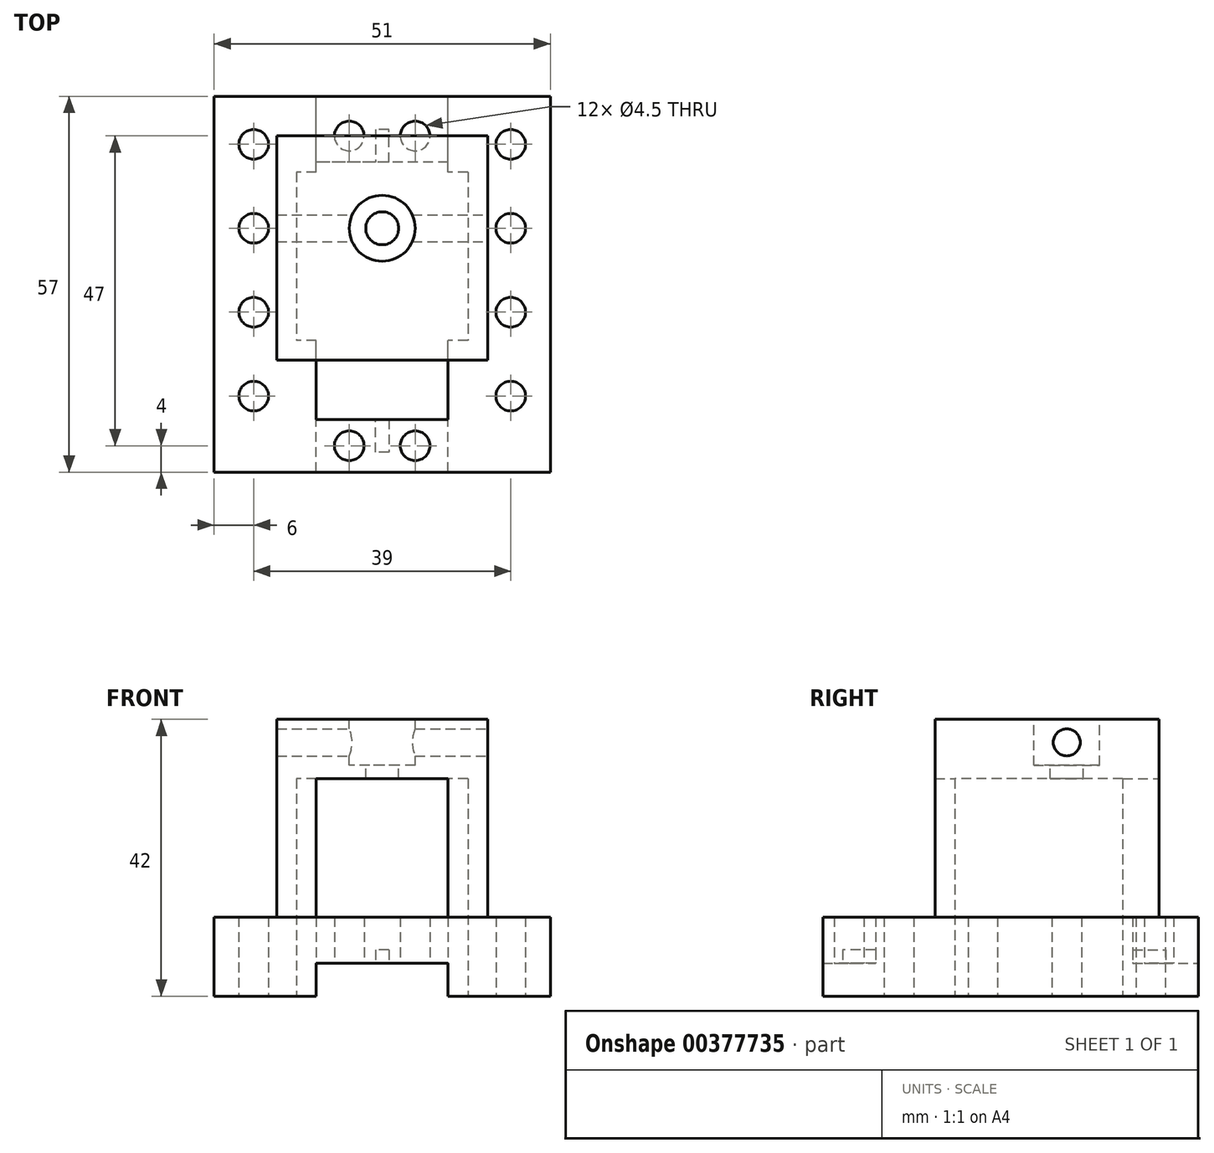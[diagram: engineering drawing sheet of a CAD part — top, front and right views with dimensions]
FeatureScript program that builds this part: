
annotation { "Feature Type Name" : "Feature", "Feature Type Description" : "" }
export const myFeature = defineFeature(function(context is Context, id is Id, definition is map)
    precondition{}
    {
        {
            var Q0;
            Q0=qCreatedBy(makeId("Top.planeOp"),FACE);
            var sketch = newSketch(context, id + "F0", { "sketchPlane" : qUnion([Q0])});
            skLineSegment(sketch, "E0.bottom", {"start": v(0, 0) * mm, "end": v(51, 0) * mm});
            skLineSegment(sketch, "E0.top", {"start": v(0, -55) * mm, "end": v(51, -55) * mm});
            skLineSegment(sketch, "E0.left", {"start": v(0, 0) * mm, "end": v(0, -55) * mm});
            skLineSegment(sketch, "E0.right", {"start": v(51, 0) * mm, "end": v(51, -55) * mm});
            skPoint(sketch, "E1", {"position": v(35.5, -55) * mm});
            skPoint(sketch, "E2", {"position": v(15.5, -55) * mm});
            skLineSegment(sketch, "E3", {"start": v(15.5, -55) * mm, "end": v(15.5, 0) * mm});
            skLineSegment(sketch, "E4", {"start": v(35.5, -55) * mm, "end": v(35.5, 0) * mm});
            skPoint(sketch, "E5", {"position": v(15.5, -47) * mm});
            skPoint(sketch, "E6", {"position": v(35.5, -47) * mm});
            skPoint(sketch, "E7", {"position": v(35.5, -8) * mm});
            skPoint(sketch, "E8", {"position": v(15.5, -8) * mm});
            skLineSegment(sketch, "E9", {"start": v(15.5, -47) * mm, "end": v(35.5, -47) * mm});
            skLineSegment(sketch, "E10", {"start": v(35.5, -8) * mm, "end": v(15.5, -8) * mm});
            skPoint(sketch, "E11", {"position": v(45, -55) * mm});
            skPoint(sketch, "E12", {"position": v(6, -55) * mm});
            skLineSegment(sketch, "E13", {"start": v(45, -55) * mm, "end": v(45, 0) * mm});
            skLineSegment(sketch, "E14", {"start": v(6, -55) * mm, "end": v(6, 0) * mm});
            skPoint(sketch, "E15", {"position": v(45, -18) * mm});
            skPoint(sketch, "E16", {"position": v(45, -30.73) * mm});
            skPoint(sketch, "E17", {"position": v(45, -5.27) * mm});
            skPoint(sketch, "E18", {"position": v(6, -18) * mm});
            skPoint(sketch, "E19", {"position": v(45, -43.46) * mm});
            skPoint(sketch, "E20", {"position": v(6, -43.46) * mm});
            skPoint(sketch, "E21", {"position": v(6, -30.73) * mm});
            skPoint(sketch, "E22", {"position": v(6, -5.27) * mm});
            skCircle(sketch, "E23", {"center": v(45, -43.46) * mm, "radius": 2.25 * mm});
            skCircle(sketch, "E24", {"center": v(45, -30.73) * mm, "radius": 2.25 * mm});
            skCircle(sketch, "E25", {"center": v(45, -18) * mm, "radius": 2.25 * mm});
            skCircle(sketch, "E26", {"center": v(45, -5.27) * mm, "radius": 2.25 * mm});
            skCircle(sketch, "E27", {"center": v(6, -43.46) * mm, "radius": 2.25 * mm});
            skCircle(sketch, "E28", {"center": v(6, -30.73) * mm, "radius": 2.25 * mm});
            skCircle(sketch, "E29", {"center": v(6, -18) * mm, "radius": 2.25 * mm});
            skCircle(sketch, "E30", {"center": v(6, -5.27) * mm, "radius": 2.25 * mm});
            skPoint(sketch, "E31", {"position": v(35.5, -9.5) * mm});
            skPoint(sketch, "E32", {"position": v(15.5, -9.5) * mm});
            skPoint(sketch, "E33", {"position": v(35.5, -35) * mm});
            skPoint(sketch, "E34", {"position": v(15.5, -35) * mm});
            skPoint(sketch, "E35", {"position": v(38.5, -9.5) * mm});
            skPoint(sketch, "E36", {"position": v(12.5, -35) * mm});
            skLineSegment(sketch, "E37.bottom", {"start": v(38.5, -9.5) * mm, "end": v(12.5, -9.5) * mm});
            skLineSegment(sketch, "E37.top", {"start": v(38.5, -35) * mm, "end": v(12.5, -35) * mm});
            skLineSegment(sketch, "E37.left", {"start": v(38.5, -9.5) * mm, "end": v(38.5, -35) * mm});
            skLineSegment(sketch, "E37.right", {"start": v(12.5, -9.5) * mm, "end": v(12.5, -35) * mm});
            skSolve(sketch);
        }
        {
            var Q0;
            {var subQ5=sQuery(id+"F0.wireOp",EDGE,"E10");Q0=makeQuery(id+"F0.imprint","IMPRINT",FACE,{"disambiguationData":[TD([[makeQuery(id+"F0.imprint","IMPRINT",EDGE,{"derivedFrom":subQ5}),-1.0]])]});}
            var Q1;
            {var subQ5=sQuery(id+"F0.wireOp",EDGE,"E9");Q1=makeQuery(id+"F0.imprint","IMPRINT",FACE,{"disambiguationData":[TD([[makeQuery(id+"F0.imprint","IMPRINT",EDGE,{"derivedFrom":subQ5}),-1.0]])]});}
            var Q2;
            {var subQ0=sQuery(id+"F0.wireOp",EDGE,"E0.left");Q2=makeQuery(id+"F0.imprint","IMPRINT",FACE,{"disambiguationData":[TD([[makeQuery(id+"F0.imprint","IMPRINT",EDGE,{"derivedFrom":subQ0}),1.0]])]});}
            var Q3;
            {var subQ4=sQuery(id+"F0.wireOp",EDGE,"E0.right");Q3=makeQuery(id+"F0.imprint","IMPRINT",FACE,{"disambiguationData":[TD([[makeQuery(id+"F0.imprint","IMPRINT",EDGE,{"derivedFrom":subQ4}),-1.0]])]});}
            var Q4;
            {var subQ1=sQuery(id+"F0.wireOp",EDGE,"E0.bottom");var subQ5=sQuery(id+"F0.wireOp",EDGE,"E3");var subQ6=makeQuery(id+"F0.imprint","INTERSECT",VERTEX,{"derivedFrom":[subQ1,subQ5]});Q4=makeQuery(id+"F0.imprint","IMPRINT",FACE,{"disambiguationData":[TD([[makeQuery(id+"F0.imprint","IMPRINT",EDGE,{"disambiguationData":[TD([[subQ6,1.0]])],"derivedFrom":subQ1}),-1.0]])]});}
            var Q5;
            {var subQ11=sQuery(id+"F0.wireOp",EDGE,"E0.bottom");var subQ15=sQuery(id+"F0.wireOp",EDGE,"E4");var subQ16=makeQuery(id+"F0.imprint","INTERSECT",VERTEX,{"derivedFrom":[subQ11,subQ15]});Q5=makeQuery(id+"F0.imprint","IMPRINT",FACE,{"disambiguationData":[TD([[makeQuery(id+"F0.imprint","IMPRINT",EDGE,{"disambiguationData":[TD([[subQ16,-1.0]])],"derivedFrom":subQ11}),-1.0]])]});}
            extrude(context, id + "F1", {"entities" : qUnion([Q0, Q1, Q2, Q3, Q4, Q5]), "depth" : 12 * mm});
        }
        {
            var Q0;
            {var subQ5=sQuery(id+"F0.wireOp",EDGE,"E9");Q0=makeQuery(id+"F0.imprint","IMPRINT",FACE,{"disambiguationData":[TD([[makeQuery(id+"F0.imprint","IMPRINT",EDGE,{"derivedFrom":subQ5}),-1.0]])]});}
            extrude(context, id + "F2", {"entities" : qUnion([Q0]), "operationType" : NewBodyOperationType.REMOVE, "depth" : 5 * mm});
        }
        {
            var Q0;
            {var subQ5=sQuery(id+"F0.wireOp",EDGE,"E10");Q0=makeQuery(id+"F0.imprint","IMPRINT",FACE,{"disambiguationData":[TD([[makeQuery(id+"F0.imprint","IMPRINT",EDGE,{"derivedFrom":subQ5}),-1.0]])]});}
            extrude(context, id + "F3", {"entities" : qUnion([Q0]), "operationType" : NewBodyOperationType.REMOVE, "depth" : 5 * mm});
        }
        {
            var Q0;
            Q0=makeQuery(id+"F2.boolean.opBoolean","COPY",FACE,{"derivedFrom":makeQuery(id+"F2.opExtrude","CAP_FACE",FACE,{"disambiguationData":[OSD([sQuery(id+"F0.wireOp",EDGE,"E0.top"),sQuery(id+"F0.wireOp",EDGE,"E3"),sQuery(id+"F0.wireOp",EDGE,"E4"),sQuery(id+"F0.wireOp",EDGE,"E9")])],"isStart":false})});
            var sketch = newSketch(context, id + "F4", { "sketchPlane" : qUnion([Q0])});
            skLineSegment(sketch, "E38", {"start": v(25.5, 47) * mm, "end": v(26.5, 47) * mm});
            skLineSegment(sketch, "E39", {"start": v(26.5, 47) * mm, "end": v(26.5, 52) * mm});
            skLineSegment(sketch, "E40", {"start": v(26.5, 52) * mm, "end": v(24.5, 52) * mm});
            skLineSegment(sketch, "E41", {"start": v(24.5, 52) * mm, "end": v(24.5, 47) * mm});
            skLineSegment(sketch, "E42", {"start": v(24.5, 47) * mm, "end": v(25.5, 47) * mm});
            skPoint(sketch, "E43", {"position": v(30.5, 55) * mm});
            skPoint(sketch, "E44", {"position": v(20.5, 55) * mm});
            skPoint(sketch, "E45", {"position": v(30.5, 51) * mm});
            skPoint(sketch, "E46", {"position": v(20.5, 51) * mm});
            skCircle(sketch, "E47", {"center": v(30.5, 51) * mm, "radius": 2.25 * mm});
            skCircle(sketch, "E48", {"center": v(20.5, 51) * mm, "radius": 2.25 * mm});
            skSolve(sketch);
        }
        {
            var Q0;
            Q0=makeQuery(id+"F4.imprint","IMPRINT",FACE,{"disambiguationData":[TD([[makeQuery(id+"F4.imprint","IMPRINT",EDGE,{"derivedFrom":sQuery(id+"F4.wireOp",EDGE,"E38")}),1.0]])]});
            extrude(context, id + "F5", {"entities" : qUnion([Q0]), "operationType" : NewBodyOperationType.REMOVE, "oppositeDirection" : true, "depth" : 2 * mm});
        }
        {
            var Q0;
            Q0=makeQuery(id+"F4.imprint","IMPRINT",FACE,{"disambiguationData":[TD([[makeQuery(id+"F4.imprint","IMPRINT",EDGE,{"derivedFrom":sQuery(id+"F4.wireOp",EDGE,"E48")}),1.0]])]});
            var Q1;
            Q1=makeQuery(id+"F4.imprint","IMPRINT",FACE,{"disambiguationData":[TD([[makeQuery(id+"F4.imprint","IMPRINT",EDGE,{"derivedFrom":sQuery(id+"F4.wireOp",EDGE,"E47")}),1.0]])]});
            extrude(context, id + "F6", {"entities" : qUnion([Q0, Q1]), "operationType" : NewBodyOperationType.REMOVE, "oppositeDirection" : true, "depth" : 25 * mm});
        }
        {
            var Q0;
            Q0=makeQuery(id+"F3.boolean.opBoolean","COPY",FACE,{"derivedFrom":makeQuery(id+"F3.opExtrude","CAP_FACE",FACE,{"disambiguationData":[OSD([sQuery(id+"F0.wireOp",EDGE,"E0.bottom"),sQuery(id+"F0.wireOp",EDGE,"E3"),sQuery(id+"F0.wireOp",EDGE,"E4"),sQuery(id+"F0.wireOp",EDGE,"E10")])],"isStart":false})});
            var sketch = newSketch(context, id + "F7", { "sketchPlane" : qUnion([Q0])});
            skLineSegment(sketch, "E49", {"start": v(25.5, 8) * mm, "end": v(26.5, 8) * mm});
            skLineSegment(sketch, "E50", {"start": v(26.5, 8) * mm, "end": v(26.5, 3) * mm});
            skLineSegment(sketch, "E51", {"start": v(26.5, 3) * mm, "end": v(24.5, 3) * mm});
            skLineSegment(sketch, "E52", {"start": v(24.5, 3) * mm, "end": v(24.5, 8) * mm});
            skLineSegment(sketch, "E53", {"start": v(24.5, 8) * mm, "end": v(25.5, 8) * mm});
            skPoint(sketch, "E54", {"position": v(30.5, 8) * mm});
            skPoint(sketch, "E55", {"position": v(20.5, 8) * mm});
            skPoint(sketch, "E56", {"position": v(30.5, 4) * mm});
            skPoint(sketch, "E57", {"position": v(20.5, 4) * mm});
            skCircle(sketch, "E58", {"center": v(20.5, 4) * mm, "radius": 2.25 * mm});
            skCircle(sketch, "E59", {"center": v(30.5, 4) * mm, "radius": 2.25 * mm});
            skSolve(sketch);
        }
        {
            var Q0;
            Q0=makeQuery(id+"F7.imprint","IMPRINT",FACE,{"disambiguationData":[TD([[makeQuery(id+"F7.imprint","IMPRINT",EDGE,{"derivedFrom":sQuery(id+"F7.wireOp",EDGE,"E49")}),1.0]])]});
            extrude(context, id + "F8", {"entities" : qUnion([Q0]), "operationType" : NewBodyOperationType.REMOVE, "oppositeDirection" : true, "depth" : 2 * mm});
        }
        {
            var Q0;
            Q0=makeQuery(id+"F7.imprint","IMPRINT",FACE,{"disambiguationData":[TD([[makeQuery(id+"F7.imprint","IMPRINT",EDGE,{"derivedFrom":sQuery(id+"F7.wireOp",EDGE,"E59")}),1.0]])]});
            var Q1;
            Q1=makeQuery(id+"F7.imprint","IMPRINT",FACE,{"disambiguationData":[TD([[makeQuery(id+"F7.imprint","IMPRINT",EDGE,{"derivedFrom":sQuery(id+"F7.wireOp",EDGE,"E58")}),1.0]])]});
            extrude(context, id + "F9", {"entities" : qUnion([Q0, Q1]), "operationType" : NewBodyOperationType.REMOVE, "oppositeDirection" : true, "depth" : 25 * mm});
        }
        {
            var Q0;
            Q0=makeQuery(id+"F1.opExtrude","CAP_FACE",FACE,{"disambiguationData":[OSD([sQuery(id+"F0.wireOp",EDGE,"E0.bottom"),sQuery(id+"F0.wireOp",EDGE,"E0.top"),sQuery(id+"F0.wireOp",EDGE,"E0.left"),sQuery(id+"F0.wireOp",EDGE,"E0.right"),sQuery(id+"F0.wireOp",EDGE,"E3"),sQuery(id+"F0.wireOp",EDGE,"E4"),sQuery(id+"F0.wireOp",EDGE,"E9"),sQuery(id+"F0.wireOp",EDGE,"E10"),sQuery(id+"F0.wireOp",EDGE,"E23"),sQuery(id+"F0.wireOp",EDGE,"E24"),sQuery(id+"F0.wireOp",EDGE,"E25"),sQuery(id+"F0.wireOp",EDGE,"E26"),sQuery(id+"F0.wireOp",EDGE,"E27"),sQuery(id+"F0.wireOp",EDGE,"E28"),sQuery(id+"F0.wireOp",EDGE,"E29"),sQuery(id+"F0.wireOp",EDGE,"E30")])],"isStart":false});
            var sketch = newSketch(context, id + "F10", { "sketchPlane" : qUnion([Q0])});
            skPoint(sketch, "E60", {"position": v(9.5, 0) * mm});
            skPoint(sketch, "E61", {"position": v(41.5, 0) * mm});
            skLineSegment(sketch, "E62", {"start": v(41.5, 0) * mm, "end": v(41.5, -55) * mm});
            skLineSegment(sketch, "E63", {"start": v(9.5, 0) * mm, "end": v(9.5, -55) * mm});
            skLineSegment(sketch, "E64", {"start": v(35.5, -55) * mm, "end": v(35.5, 0) * mm});
            skLineSegment(sketch, "E65", {"start": v(15.5, -55) * mm, "end": v(15.5, 0) * mm});
            skSolve(sketch);
        }
        {
            var Q0;
            {var subQ4=sQuery(id+"F10.wireOp",EDGE,"E62");Q0=makeQuery(id+"F10.imprint","IMPRINT",FACE,{"disambiguationData":[TD([[makeQuery(id+"F10.imprint","IMPRINT",EDGE,{"derivedFrom":subQ4}),-1.0]])]});}
            var Q1;
            {var subQ7=sQuery(id+"F10.wireOp",EDGE,"E63");Q1=makeQuery(id+"F10.imprint","IMPRINT",FACE,{"disambiguationData":[TD([[makeQuery(id+"F10.imprint","IMPRINT",EDGE,{"derivedFrom":subQ7}),1.0]])]});}
            extrude(context, id + "F11", {"entities" : qUnion([Q0, Q1]), "operationType" : NewBodyOperationType.ADD, "depth" : 30 * mm});
        }
        {
            var Q0;
            {var subQ0=sQuery(id+"F0.wireOp",EDGE,"E0.bottom");var subQ1=makeQuery(id+"F1.opExtrude","CAP_EDGE",EDGE,{"disambiguationData":[OSD([subQ0])],"isStart":false});Q0=makeQuery(id+"F11.boolean.opBoolean","MERGE",FACE,{"derivedFrom":[makeQuery(id+"F1.opExtrude","SWEPT_FACE",FACE,{"disambiguationData":[OSD([subQ0])]}),makeQuery(id+"F11.opExtrude","SWEPT_FACE",FACE,{"disambiguationData":[OSD([subQ0]),TDD([makeQuery(id+"F10.imprint","IMPRINT",EDGE,{"disambiguationData":[TD([[makeQuery(id+"F10.imprint","INTERSECT",VERTEX,{"derivedFrom":[subQ1,sQuery(id+"F10.wireOp",EDGE,"E62")]}),1.0]])],"derivedFrom":subQ1})])]}),makeQuery(id+"F11.opExtrude","SWEPT_FACE",FACE,{"disambiguationData":[OSD([subQ0]),TDD([makeQuery(id+"F10.imprint","IMPRINT",EDGE,{"disambiguationData":[TD([[makeQuery(id+"F10.imprint","INTERSECT",VERTEX,{"derivedFrom":[subQ1,sQuery(id+"F10.wireOp",EDGE,"E63")]}),-1.0]])],"derivedFrom":subQ1})])]})]});}
            var sketch = newSketch(context, id + "F12", { "sketchPlane" : qUnion([Q0])});
            skLineSegment(sketch, "E66", {"start": v(-41.5, 12) * mm, "end": v(-35.5, 12) * mm});
            skLineSegment(sketch, "E67", {"start": v(-15.5, 12) * mm, "end": v(-9.5, 12) * mm});
            skSolve(sketch);
        }
        {
            var Q0;
            Q0 = qSketchRegion(id + "F12", true);
            var Q1;
            Q1=makeQuery(id+"F12.imprint","IMPRINT",FACE,{"disambiguationData":[TD([[makeQuery(id+"F12.imprint","IMPRINT",EDGE,{"derivedFrom":sQuery(id+"F12.wireOp",EDGE,"E66")}),1.0]])]});
            var Q2;
            Q2=makeQuery(id+"F12.imprint","IMPRINT",FACE,{"disambiguationData":[TD([[makeQuery(id+"F12.imprint","IMPRINT",EDGE,{"derivedFrom":sQuery(id+"F12.wireOp",EDGE,"E67")}),1.0]])]});
            extrude(context, id + "F13", {"entities" : qUnion([Q0, Q1, Q2]), "operationType" : NewBodyOperationType.REMOVE, "oppositeDirection" : true, "depth" : 4 * mm});
        }
        {
            var Q0;
            {var subQ0=sQuery(id+"F0.wireOp",EDGE,"E0.top");var subQ1=makeQuery(id+"F1.opExtrude","CAP_EDGE",EDGE,{"disambiguationData":[OSD([subQ0])],"isStart":false});Q0=makeQuery(id+"F11.boolean.opBoolean","MERGE",FACE,{"derivedFrom":[makeQuery(id+"F1.opExtrude","SWEPT_FACE",FACE,{"disambiguationData":[OSD([subQ0])]}),makeQuery(id+"F11.opExtrude","SWEPT_FACE",FACE,{"disambiguationData":[OSD([subQ0]),TDD([makeQuery(id+"F10.imprint","IMPRINT",EDGE,{"disambiguationData":[TD([[makeQuery(id+"F10.imprint","INTERSECT",VERTEX,{"derivedFrom":[subQ1,sQuery(id+"F10.wireOp",EDGE,"E62")]}),1.0]])],"derivedFrom":subQ1})])]}),makeQuery(id+"F11.opExtrude","SWEPT_FACE",FACE,{"disambiguationData":[OSD([subQ0]),TDD([makeQuery(id+"F10.imprint","IMPRINT",EDGE,{"disambiguationData":[TD([[makeQuery(id+"F10.imprint","INTERSECT",VERTEX,{"derivedFrom":[subQ1,sQuery(id+"F10.wireOp",EDGE,"E63")]}),-1.0]])],"derivedFrom":subQ1})])]})]});}
            var sketch = newSketch(context, id + "F14", { "sketchPlane" : qUnion([Q0])});
            skLineSegment(sketch, "E68", {"start": v(9.5, 12) * mm, "end": v(15.5, 12) * mm});
            skLineSegment(sketch, "E69", {"start": v(35.5, 12) * mm, "end": v(41.5, 12) * mm});
            skSolve(sketch);
        }
        {
            var Q0;
            Q0 = qSketchRegion(id + "F14", true);
            var Q1;
            Q1=makeQuery(id+"F14.imprint","IMPRINT",FACE,{"disambiguationData":[TD([[makeQuery(id+"F14.imprint","IMPRINT",EDGE,{"derivedFrom":sQuery(id+"F14.wireOp",EDGE,"E68")}),1.0]])]});
            var Q2;
            Q2=makeQuery(id+"F14.imprint","IMPRINT",FACE,{"disambiguationData":[TD([[makeQuery(id+"F14.imprint","IMPRINT",EDGE,{"derivedFrom":sQuery(id+"F14.wireOp",EDGE,"E69")}),1.0]])]});
            extrude(context, id + "F15", {"entities" : qUnion([Q0, Q1, Q2]), "operationType" : NewBodyOperationType.REMOVE, "oppositeDirection" : true, "depth" : 4 * mm});
        }
        {
            var Q0;
            Q0=makeQuery(id+"F11.opExtrude","CAP_FACE",FACE,{"disambiguationData":[OSD([sQuery(id+"F0.wireOp",EDGE,"E0.bottom"),sQuery(id+"F0.wireOp",EDGE,"E0.top"),sQuery(id+"F0.wireOp",EDGE,"E37.bottom"),sQuery(id+"F0.wireOp",EDGE,"E37.top"),sQuery(id+"F0.wireOp",EDGE,"E37.left"),sQuery(id+"F10.wireOp",EDGE,"E62"),sQuery(id+"F10.wireOp",EDGE,"E64")])],"isStart":false});
            var sketch = newSketch(context, id + "F16", { "sketchPlane" : qUnion([Q0])});
            skPoint(sketch, "E70.oppositeSnap0", {"position": v(38.5, -51) * mm});
            skLineSegment(sketch, "E70.bottom", {"start": v(41.5, -4) * mm, "end": v(9.5, -4) * mm});
            skLineSegment(sketch, "E70.top", {"start": v(41.5, -51) * mm, "end": v(9.5, -51) * mm});
            skLineSegment(sketch, "E70.left", {"start": v(41.5, -4) * mm, "end": v(41.5, -51) * mm});
            skLineSegment(sketch, "E70.right", {"start": v(9.5, -4) * mm, "end": v(9.5, -51) * mm});
            skSolve(sketch);
        }
        {
            var Q0;
            Q0 = qSketchRegion(id + "F16", true);
            extrude(context, id + "F17", {"entities" : qUnion([Q0]), "operationType" : NewBodyOperationType.ADD, "oppositeDirection" : true, "depth" : 9 * mm});
        }
        {
            var Q0;
            {var subQ0=sQuery(id+"F0.wireOp",EDGE,"E37.top");var subQ1=sQuery(id+"F0.wireOp",EDGE,"E37.bottom");var subQ2=sQuery(id+"F0.wireOp",EDGE,"E0.top");var subQ3=sQuery(id+"F0.wireOp",EDGE,"E0.bottom");Q0=makeQuery(id+"F17.boolean.opBoolean","MERGE",FACE,{"derivedFrom":[makeQuery(id+"F11.opExtrude","CAP_FACE",FACE,{"disambiguationData":[OSD([subQ3,subQ2,subQ1,subQ0,sQuery(id+"F0.wireOp",EDGE,"E37.left"),sQuery(id+"F10.wireOp",EDGE,"E62"),sQuery(id+"F10.wireOp",EDGE,"E64")])],"isStart":false}),makeQuery(id+"F11.opExtrude","CAP_FACE",FACE,{"disambiguationData":[OSD([subQ3,subQ2,subQ1,subQ0,sQuery(id+"F0.wireOp",EDGE,"E37.right"),sQuery(id+"F10.wireOp",EDGE,"E63"),sQuery(id+"F10.wireOp",EDGE,"E65")])],"isStart":false}),makeQuery(id+"F17.opExtrude","CAP_FACE",FACE,{"disambiguationData":[OSD([sQuery(id+"F16.wireOp",EDGE,"E70.bottom"),sQuery(id+"F16.wireOp",EDGE,"E70.top"),sQuery(id+"F16.wireOp",EDGE,"E70.left"),sQuery(id+"F16.wireOp",EDGE,"E70.right")])],"isStart":true})]});}
            var sketch = newSketch(context, id + "F18", { "sketchPlane" : qUnion([Q0])});
            skPoint(sketch, "E71", {"position": v(25.5, -18) * mm});
            skPoint(sketch, "E71.positionSnap0", {"position": v(25.5, -4) * mm});
            skCircle(sketch, "E72", {"center": v(25.5, -18) * mm, "radius": 5 * mm});
            skCircle(sketch, "E73", {"center": v(25.5, -18) * mm, "radius": 2.5 * mm});
            skSolve(sketch);
        }
        {
            var Q0;
            Q0=makeQuery(id+"F18.imprint","IMPRINT",FACE,{"disambiguationData":[TD([[makeQuery(id+"F18.imprint","IMPRINT",EDGE,{"derivedFrom":sQuery(id+"F18.wireOp",EDGE,"E72")}),1.0]])]});
            extrude(context, id + "F19", {"entities" : qUnion([Q0]), "operationType" : NewBodyOperationType.REMOVE, "oppositeDirection" : true, "depth" : 7 * mm});
        }
        {
            var Q0;
            {var subQ0=sQuery(id+"F0.wireOp",EDGE,"E37.top");var subQ1=sQuery(id+"F0.wireOp",EDGE,"E37.bottom");var subQ2=sQuery(id+"F0.wireOp",EDGE,"E0.top");var subQ3=sQuery(id+"F0.wireOp",EDGE,"E0.bottom");Q0=makeQuery(id+"F19.boolean.opBoolean","SPLIT",FACE,{"disambiguationData":[TD([makeQuery(id+"F19.opExtrude","SWEPT_FACE",FACE,{"disambiguationData":[OSD([sQuery(id+"F18.wireOp",EDGE,"E73")])]})])],"derivedFrom":makeQuery(id+"F17.boolean.opBoolean","MERGE",FACE,{"derivedFrom":[makeQuery(id+"F11.opExtrude","CAP_FACE",FACE,{"disambiguationData":[OSD([subQ3,subQ2,subQ1,subQ0,sQuery(id+"F0.wireOp",EDGE,"E37.left"),sQuery(id+"F10.wireOp",EDGE,"E62"),sQuery(id+"F10.wireOp",EDGE,"E64")])],"isStart":false}),makeQuery(id+"F11.opExtrude","CAP_FACE",FACE,{"disambiguationData":[OSD([subQ3,subQ2,subQ1,subQ0,sQuery(id+"F0.wireOp",EDGE,"E37.right"),sQuery(id+"F10.wireOp",EDGE,"E63"),sQuery(id+"F10.wireOp",EDGE,"E65")])],"isStart":false}),makeQuery(id+"F17.opExtrude","CAP_FACE",FACE,{"disambiguationData":[OSD([sQuery(id+"F16.wireOp",EDGE,"E70.bottom"),sQuery(id+"F16.wireOp",EDGE,"E70.top"),sQuery(id+"F16.wireOp",EDGE,"E70.left"),sQuery(id+"F16.wireOp",EDGE,"E70.right")])],"isStart":true})]})});}
            extrude(context, id + "F20", {"entities" : qUnion([Q0]), "operationType" : NewBodyOperationType.REMOVE, "oppositeDirection" : true, "depth" : 25 * mm});
        }
        {
            var Q0;
            Q0=makeQuery(id+"F11.opExtrude","SWEPT_FACE",FACE,{"disambiguationData":[OSD([sQuery(id+"F10.wireOp",EDGE,"E62")])]});
            var sketch = newSketch(context, id + "F21", { "sketchPlane" : qUnion([Q0])});
            skPoint(sketch, "E74", {"position": v(-18, 42) * mm});
            skPoint(sketch, "E75", {"position": v(-18, 38.5) * mm});
            skCircle(sketch, "E76", {"center": v(-18, 38.5) * mm, "radius": 2.05 * mm});
            skSolve(sketch);
        }
        {
            var Q0;
            Q0 = qSketchRegion(id + "F21", true);
            extrude(context, id + "F22", {"entities" : qUnion([Q0]), "operationType" : NewBodyOperationType.REMOVE, "oppositeDirection" : true, "depth" : 58 * mm});
        }
        {
            var Q0;
            {var subQ0=sQuery(id+"F0.wireOp",EDGE,"E0.top");Q0=makeQuery(id+"F17.boolean.opBoolean","MERGE",FACE,{"derivedFrom":[makeQuery(id+"F15.boolean.opBoolean","COPY",FACE,{"derivedFrom":makeQuery(id+"F15.opExtrude","CAP_FACE",FACE,{"disambiguationData":[OSD([subQ0,sQuery(id+"F10.wireOp",EDGE,"E63"),sQuery(id+"F10.wireOp",EDGE,"E65"),sQuery(id+"F14.wireOp",EDGE,"E68")])],"isStart":false})}),makeQuery(id+"F15.boolean.opBoolean","COPY",FACE,{"derivedFrom":makeQuery(id+"F15.opExtrude","CAP_FACE",FACE,{"disambiguationData":[OSD([subQ0,sQuery(id+"F10.wireOp",EDGE,"E62"),sQuery(id+"F10.wireOp",EDGE,"E64"),sQuery(id+"F14.wireOp",EDGE,"E69")])],"isStart":false})}),makeQuery(id+"F17.opExtrude","SWEPT_FACE",FACE,{"disambiguationData":[OSD([sQuery(id+"F16.wireOp",EDGE,"E70.top")])]})]});}
            extrude(context, id + "F23", {"entities" : qUnion([Q0]), "operationType" : NewBodyOperationType.REMOVE, "oppositeDirection" : true, "depth" : 13 * mm});
        }
        {
            var Q0;
            {var subQ0=sQuery(id+"F0.wireOp",EDGE,"E0.bottom");var subQ1=makeQuery(id+"F1.opExtrude","CAP_EDGE",EDGE,{"disambiguationData":[OSD([subQ0])],"isStart":false});Q0=makeQuery(id+"F11.boolean.opBoolean","MERGE",FACE,{"derivedFrom":[makeQuery(id+"F1.opExtrude","SWEPT_FACE",FACE,{"disambiguationData":[OSD([subQ0])]}),makeQuery(id+"F11.opExtrude","SWEPT_FACE",FACE,{"disambiguationData":[OSD([subQ0]),TDD([makeQuery(id+"F10.imprint","IMPRINT",EDGE,{"disambiguationData":[TD([[makeQuery(id+"F10.imprint","INTERSECT",VERTEX,{"derivedFrom":[subQ1,sQuery(id+"F10.wireOp",EDGE,"E62")]}),1.0]])],"derivedFrom":subQ1})])]}),makeQuery(id+"F11.opExtrude","SWEPT_FACE",FACE,{"disambiguationData":[OSD([subQ0]),TDD([makeQuery(id+"F10.imprint","IMPRINT",EDGE,{"disambiguationData":[TD([[makeQuery(id+"F10.imprint","INTERSECT",VERTEX,{"derivedFrom":[subQ1,sQuery(id+"F10.wireOp",EDGE,"E63")]}),-1.0]])],"derivedFrom":subQ1})])]})]});}
            extrude(context, id + "F24", {"entities" : qUnion([Q0]), "operationType" : NewBodyOperationType.ADD, "depth" : 2 * mm});
        }
    });
